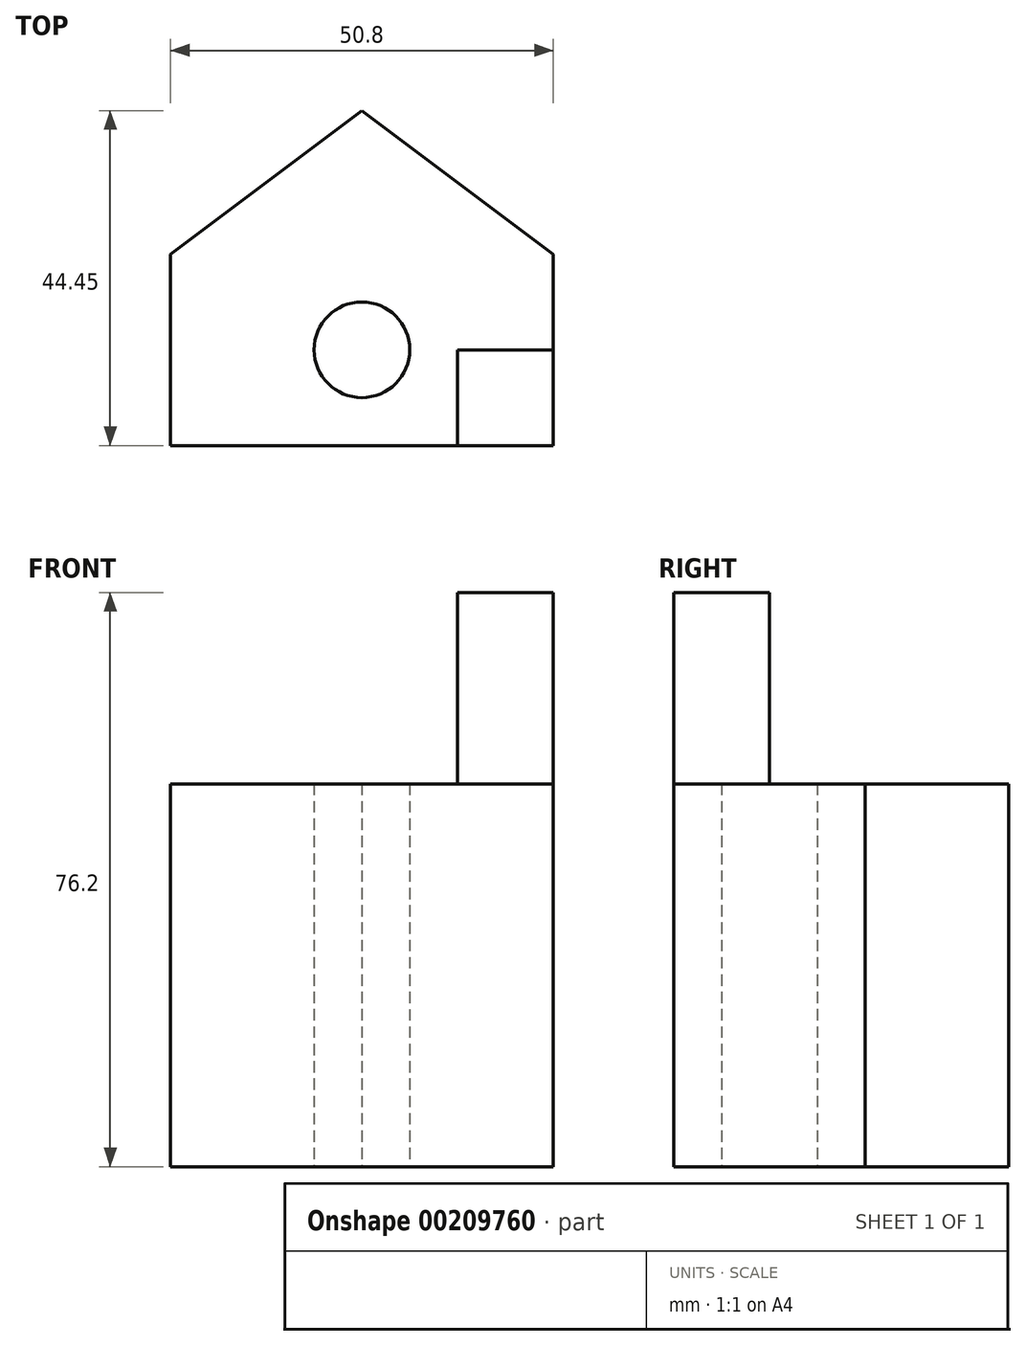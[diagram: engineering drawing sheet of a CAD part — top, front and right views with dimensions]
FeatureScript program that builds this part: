
annotation { "Feature Type Name" : "Feature", "Feature Type Description" : "" }
export const myFeature = defineFeature(function(context is Context, id is Id, definition is map)
    precondition{}
    {
        {
            var Q0;
            Q0=qCreatedBy(makeId("Top.planeOp"),FACE);
            var sketch = newSketch(context, id + "F0", { "sketchPlane" : qUnion([Q0])});
            skLineSegment(sketch, "E0.bottom", {"start": v(0, 0) * mm, "end": v(50.8, 0) * mm});
            skLineSegment(sketch, "E0.top", {"start": v(0, 25.4) * mm, "end": v(50.8, 25.4) * mm});
            skLineSegment(sketch, "E0.left", {"start": v(0, 0) * mm, "end": v(0, 25.4) * mm});
            skLineSegment(sketch, "E0.right", {"start": v(50.8, 0) * mm, "end": v(50.8, 25.4) * mm});
            skLineSegment(sketch, "E1", {"start": v(0, 25.4) * mm, "end": v(25.4, 44.45) * mm});
            skPoint(sketch, "E1.endSnap0", {"position": v(25.4, 25.4) * mm});
            skLineSegment(sketch, "E2", {"start": v(25.4, 44.45) * mm, "end": v(50.8, 25.4) * mm});
            skSolve(sketch);
        }
        {
            var Q0;
            Q0 = qSketchRegion(id + "F0", true);
            extrude(context, id + "F1", {"entities" : qUnion([Q0]), "depth" : 50.8 * mm});
        }
        {
            var Q0;
            Q0=qCreatedBy(makeId("Top.planeOp"),FACE);
            var sketch = newSketch(context, id + "F2", { "sketchPlane" : qUnion([Q0])});
            skCircle(sketch, "E3", {"center": v(25.4, 12.7) * mm, "radius": 6.35 * mm});
            skSolve(sketch);
        }
        {
            var Q0;
            Q0 = qSketchRegion(id + "F2", true);
            extrude(context, id + "F3", {"entities" : qUnion([Q0]), "operationType" : NewBodyOperationType.REMOVE, "endBound" : BoundingType.THROUGH_ALL, "depth" : 25.4 * mm});
        }
        {
            var Q0;
            Q0=makeQuery(id+"F1.opExtrude","CAP_FACE",FACE,{"disambiguationData":[OSD([sQuery(id+"F0.wireOp",EDGE,"E0.bottom"),sQuery(id+"F0.wireOp",EDGE,"E0.left"),sQuery(id+"F0.wireOp",EDGE,"E0.right"),sQuery(id+"F0.wireOp",EDGE,"E1"),sQuery(id+"F0.wireOp",EDGE,"E2")])],"isStart":false});
            var sketch = newSketch(context, id + "F4", { "sketchPlane" : qUnion([Q0])});
            skLineSegment(sketch, "E4.bottom", {"start": v(50.8, 0) * mm, "end": v(38.1, 0) * mm});
            skLineSegment(sketch, "E4.top", {"start": v(50.8, 12.7) * mm, "end": v(38.1, 12.7) * mm});
            skLineSegment(sketch, "E4.left", {"start": v(50.8, 0) * mm, "end": v(50.8, 12.7) * mm});
            skLineSegment(sketch, "E4.right", {"start": v(38.1, 0) * mm, "end": v(38.1, 12.7) * mm});
            skSolve(sketch);
        }
        {
            var Q0;
            Q0 = qSketchRegion(id + "F4", true);
            extrude(context, id + "F5", {"entities" : qUnion([Q0]), "depth" : 25.4 * mm});
        }
    });
